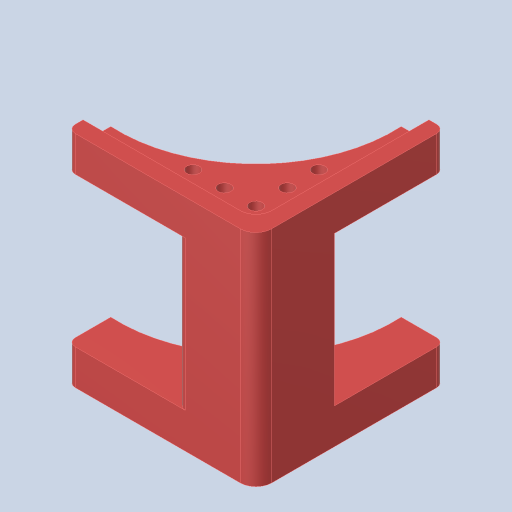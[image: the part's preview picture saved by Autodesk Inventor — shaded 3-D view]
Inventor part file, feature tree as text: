
AUTODESK INVENTOR PART (.ipt)
format: ipt  version: 2023.4 (Build 274418000, 418)  size: 283,648 bytes
history: native  units: in
note: dims shown in document units (in); Inventor stores cm internally (conversion verified against a paired STEP export)
features: extrude x8, sketch x8, projected_geometry x5, other x4, fillet x2, loft x2, hole x1
ambient origin geometry x8: Origin, YZ Plane, XZ Plane, XY Plane, X Axis, Y Axis, Z Axis, Center Point
bodies: Solid1 (feature_tree)
feature tree (30):
  extrude  "Extrusion1"  Depth=1.25in
  extrude  "Extrusion2"  Depth=0.3125in
  sketch  "Sketch4"  dims[d6=0.5in d7=0.5in]
  extrude  "Extrusion3"  Depth=0.5in
  extrude  "Extrusion4"  Depth=0.5in
  sketch  "Sketch5"  dims[d8=0.5in d9=0.5in]
  extrude  "Extrusion5"  Depth=0.3125in TaperAngle=0.0deg
  extrude  "Extrusion6"  Depth=0.5in
  sketch  "Sketch9"  dims[d13=0.5in d14=0.5in d15=0.5in]
  fillet  "Fillet2"  Radius=0.5in
  hole  "Hole1"  [1 undecoded]
  extrude  "Extrusion9"  Depth=0.125in
  sketch  "Sketch12"  dims[d18=0.1875in d19=0.0in d20=0.125in d21=0.125in d22=0.0in d23=0.25in d24=0.25in d25=1.75in d26=0.0in d27=1.75in d28=0.0in d35=0.5in d36=0.5in d37=0.5in d38=0.5in d39=0.5in d40=0.5in d41=0.25in d43=0.201in d44=0.38in d45=0.385in d46=0.25in d47=0.5635in d48=1.0in d49=0.8108in d52=0.3333in d53=0.3333in d54=0.3333in d55=0.3333in d56=0.25in d57=0.0in d60=0.25in d61=0.25in d62=2.125in d63=2.125in d64=4.375in d68=0.0in d69=90.0deg d70=0.0in d71=90.0deg d72=0.0in d73=90.0deg d74=0.0in d75=90.0deg d76=0.0in d77=0.0in d78=0.125in]
  loft  "Loft1"
  loft  "Loft2"
  extrude  "Extrusion11"  Depth=0.25in
  fillet  "Fillet7"  Radius=1.75in
  sketch  "Sketch2"  dims[d0=1.25in d1=1.25in]
  sketch  "Sketch3"  dims[d2=3.0in d3=0.0in d4=0.3125in]
  sketch  "Sketch6"  dims[d10=0.25in d11=0.3125in d12=0.0in]
  sketch  "Sketch11"  dims[d16=0.5in d17=0.25in]
  other  "Edges1"
  other  "Edges2"
  other  "Edges3"
  other  "Edges4"
  projected_geometry  "Project Cut Edges1"
  projected_geometry  "Project Cut Edges2"
  projected_geometry  "Project Cut Edges3"
  projected_geometry  "Project Cut Edges4"
  projected_geometry  "Project Cut Edges7"
note: 1 required parameter value undecoded (feature->parameter linkage not recoverable at this tier; creation-order binding heuristic only, values carry confidence <= 0.55)
